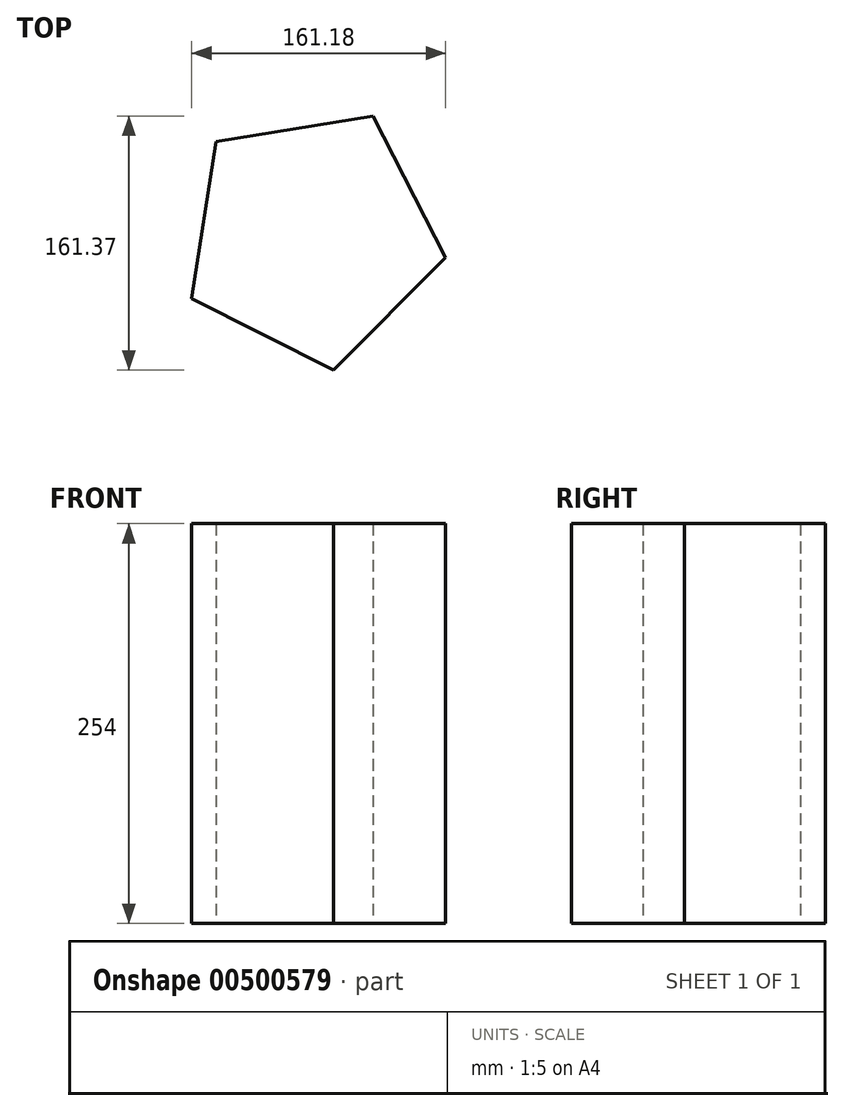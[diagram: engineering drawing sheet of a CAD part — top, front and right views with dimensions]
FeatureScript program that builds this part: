
annotation { "Feature Type Name" : "Feature", "Feature Type Description" : "" }
export const myFeature = defineFeature(function(context is Context, id is Id, definition is map)
    precondition{}
    {
        {
            var Q0;
            Q0=qCreatedBy(makeId("Top.planeOp"),FACE);
            var sketch = newSketch(context, id + "F0", { "sketchPlane" : qUnion([Q0])});
            skPoint(sketch, "E0", {"position": v(-5.54, 0) * mm});
            skCircle(sketch, "E1.cCircle", {"center": v(-5.54, 0) * mm, "radius": 85.84 * mm, "construction": true});
            skLineSegment(sketch, "E1.0", {"start": v(-66.46, 60.48) * mm, "end": v(33.16, 76.63) * mm});
            skLineSegment(sketch, "E1.1", {"start": v(33.16, 76.63) * mm, "end": v(79.3, -13.12) * mm});
            skLineSegment(sketch, "E1.2", {"start": v(79.3, -13.12) * mm, "end": v(8.2, -84.74) * mm});
            skLineSegment(sketch, "E1.3", {"start": v(8.2, -84.74) * mm, "end": v(-81.88, -39.25) * mm});
            skLineSegment(sketch, "E1.4", {"start": v(-81.88, -39.25) * mm, "end": v(-66.46, 60.48) * mm});
            skSolve(sketch);
        }
        {
            var Q0;
            Q0 = qSketchRegion(id + "F0", true);
            extrude(context, id + "F1", {"entities" : qUnion([Q0]), "depth" : 254 * mm});
        }
    });
